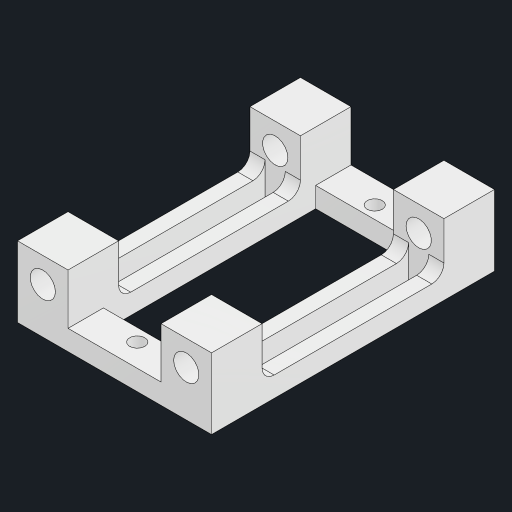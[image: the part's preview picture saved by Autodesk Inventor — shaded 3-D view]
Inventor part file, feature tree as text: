
AUTODESK INVENTOR PART (.ipt)
format: ipt  version: 2023 (Build 270158000, 158)  size: 208,896 bytes
history: native  units: in
note: dims shown in document units (in); Inventor stores cm internally (conversion verified against a paired STEP export)
features: sketch x4, extrude x4, other x3, mirror x2, hole x1, fillet x1, projected_geometry x1
ambient origin geometry x8: Origin, YZ Plane, XZ Plane, XY Plane, X Axis, Y Axis, Z Axis, Center Point
bodies: Body1 (feature_tree)
feature tree (16):
  other  "ソリッド1"
  sketch  "スケッチ1"
  extrude  "押し出し1"  Depth=0.8268in
  hole  "穴1"  [1 undecoded]
  extrude  "押し出し2"  Depth=0.1969in
  extrude  "押し出し5"  Depth=0.9252in
  mirror  "ミラー4"
  extrude  "押し出し6"  Depth=0.315in
  mirror  "ミラー5"
  fillet  "フィレット1"  Radius=0.0787in
  other  "作業平面1"
  other  "作業平面2"
  sketch  "スケッチ2"
  projected_geometry  "投影ループ1"
  sketch  "スケッチ6"
  sketch  "スケッチ7"
note: 1 required parameter value undecoded (feature->parameter linkage not recoverable at this tier; creation-order binding heuristic only, values carry confidence <= 0.55)
